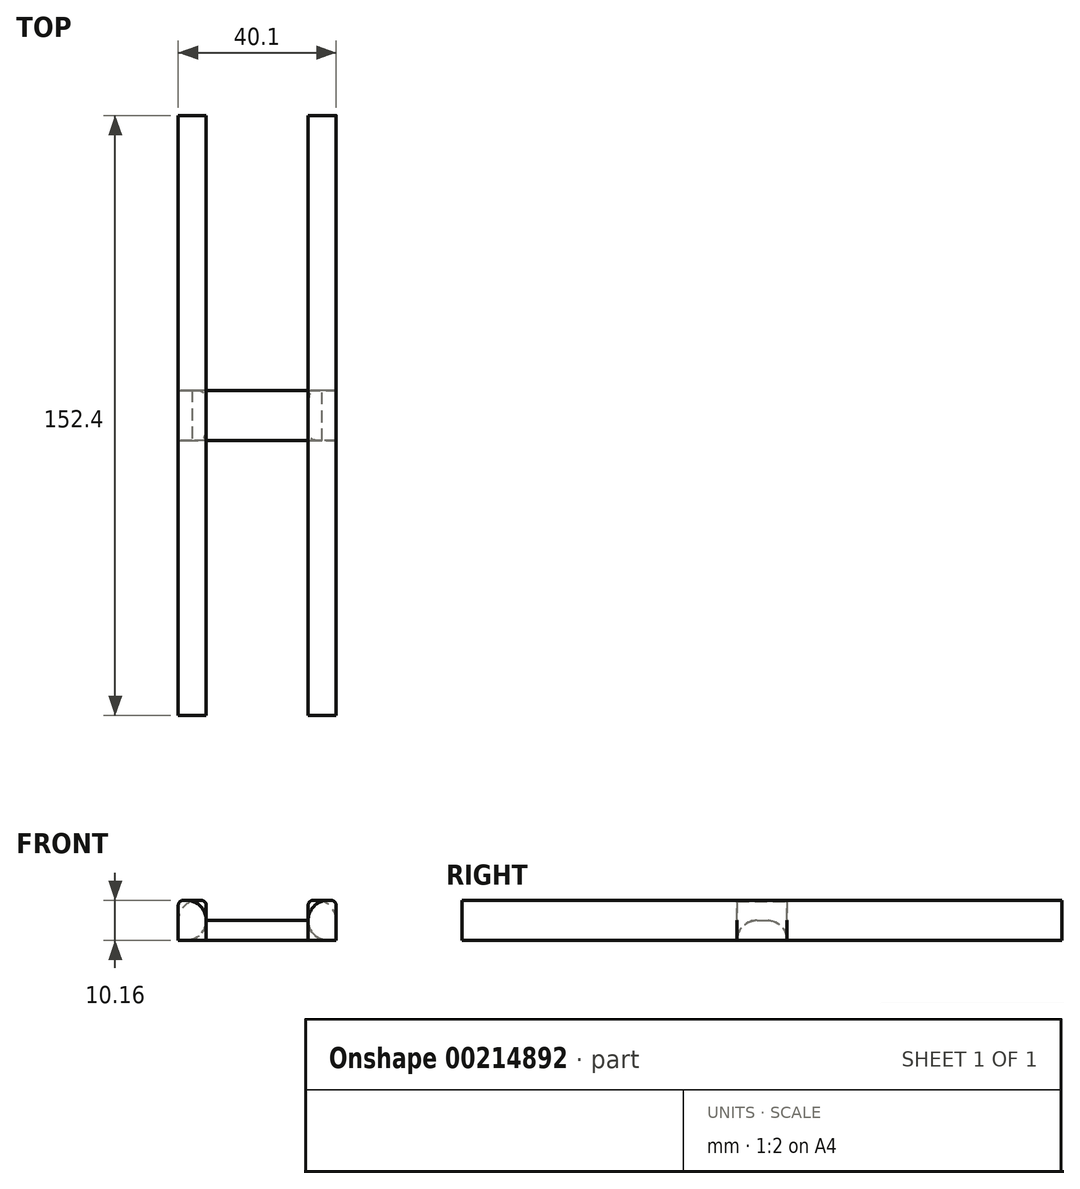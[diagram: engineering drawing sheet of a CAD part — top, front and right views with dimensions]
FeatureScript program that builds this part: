
annotation { "Feature Type Name" : "Feature", "Feature Type Description" : "" }
export const myFeature = defineFeature(function(context is Context, id is Id, definition is map)
    precondition{}
    {
        {
            var Q0;
            Q0=qCreatedBy(makeId("Front.planeOp"),FACE);
            var sketch = newSketch(context, id + "F0", { "sketchPlane" : qUnion([Q0])});
            skLineSegment(sketch, "E0.bottom", {"start": v(-45.7, 10.16) * mm, "end": v(-38.59, 10.16) * mm});
            skLineSegment(sketch, "E0.top", {"start": v(-45.7, 0) * mm, "end": v(-38.59, 0) * mm});
            skLineSegment(sketch, "E0.left", {"start": v(-45.7, 10.16) * mm, "end": v(-45.7, 0) * mm});
            skLineSegment(sketch, "E0.right", {"start": v(-38.59, 10.16) * mm, "end": v(-38.59, 0) * mm});
            skLineSegment(sketch, "E1.bottom", {"start": v(-38.59, 5.08) * mm, "end": v(-12.71, 5.08) * mm});
            skLineSegment(sketch, "E1.top", {"start": v(-38.59, 0) * mm, "end": v(-12.71, 0) * mm});
            skLineSegment(sketch, "E1.left", {"start": v(-38.59, 5.08) * mm, "end": v(-38.59, 0) * mm});
            skLineSegment(sketch, "E1.right", {"start": v(-12.71, 5.08) * mm, "end": v(-12.71, 0) * mm});
            skLineSegment(sketch, "E2.bottom", {"start": v(-12.71, 0) * mm, "end": v(-5.6, 0) * mm});
            skLineSegment(sketch, "E2.top", {"start": v(-12.71, 10.16) * mm, "end": v(-5.6, 10.16) * mm});
            skLineSegment(sketch, "E2.left", {"start": v(-12.71, 0) * mm, "end": v(-12.71, 10.16) * mm});
            skLineSegment(sketch, "E2.right", {"start": v(-5.6, 0) * mm, "end": v(-5.6, 10.16) * mm});
            skSolve(sketch);
        }
        {
            var Q0;
            Q0=makeQuery(id+"F0.imprint","IMPRINT",FACE,{"disambiguationData":[TD([[makeQuery(id+"F0.imprint","IMPRINT",EDGE,{"derivedFrom":sQuery(id+"F0.wireOp",EDGE,"E0.bottom")}),-1.0]])]});
            var Q1;
            {var subQ3=sQuery(id+"F0.wireOp",EDGE,"E2.bottom");Q1=makeQuery(id+"F0.imprint","IMPRINT",FACE,{"disambiguationData":[TD([[makeQuery(id+"F0.imprint","IMPRINT",EDGE,{"derivedFrom":subQ3}),1.0]])]});}
            extrude(context, id + "F1", {"entities" : qUnion([Q0, Q1]), "endBound" : BoundingType.SYMMETRIC, "depth" : 152.4 * mm});
        }
        {
            var Q0;
            Q0 = qSketchRegion(id + "F0", true);
            extrude(context, id + "F2", {"entities" : qUnion([Q0]), "endBound" : BoundingType.SYMMETRIC, "depth" : 12.7 * mm});
        }
        {
            var Q0;
            Q0=makeQuery(id+"F1.opExtrude","SWEPT_EDGE",EDGE,{"disambiguationData":[OSD([sQuery(id+"F0.wireOp",EDGE,"E0.bottom"),sQuery(id+"F0.wireOp",EDGE,"E0.left")])]});
            var Q1;
            Q1=makeQuery(id+"F1.opExtrude","SWEPT_EDGE",EDGE,{"disambiguationData":[OSD([sQuery(id+"F0.wireOp",EDGE,"E0.bottom"),sQuery(id+"F0.wireOp",EDGE,"E0.right")])]});
            var Q2;
            Q2=makeQuery(id+"F1.opExtrude","SWEPT_EDGE",EDGE,{"disambiguationData":[OSD([sQuery(id+"F0.wireOp",EDGE,"E2.top"),sQuery(id+"F0.wireOp",EDGE,"E2.left")])]});
            var Q3;
            Q3=makeQuery(id+"F1.opExtrude","SWEPT_EDGE",EDGE,{"disambiguationData":[OSD([sQuery(id+"F0.wireOp",EDGE,"E2.top"),sQuery(id+"F0.wireOp",EDGE,"E2.right")])]});
            fillet(context, id + "F3", {"entities" : qUnion([Q0, Q1, Q2, Q3]), "radius" : 1.27 * mm, "tangentPropagation" : true, "allowEdgeOverflow" : false});
        }
        {
            var Q0;
            Q0=makeQuery(id+"F2.opExtrude","SWEPT_EDGE",EDGE,{"disambiguationData":[OSD([sQuery(id+"F0.wireOp",EDGE,"E0.bottom"),sQuery(id+"F0.wireOp",EDGE,"E0.left")])]});
            var Q1;
            Q1=makeQuery(id+"F2.opExtrude","SWEPT_EDGE",EDGE,{"disambiguationData":[OSD([sQuery(id+"F0.wireOp",EDGE,"E0.bottom"),sQuery(id+"F0.wireOp",EDGE,"E0.right")])]});
            var Q2;
            Q2=makeQuery(id+"F2.opExtrude","SWEPT_EDGE",EDGE,{"disambiguationData":[OSD([sQuery(id+"F0.wireOp",EDGE,"E2.top"),sQuery(id+"F0.wireOp",EDGE,"E2.left")])]});
            var Q3;
            Q3=makeQuery(id+"F2.opExtrude","SWEPT_EDGE",EDGE,{"disambiguationData":[OSD([sQuery(id+"F0.wireOp",EDGE,"E2.top"),sQuery(id+"F0.wireOp",EDGE,"E2.right")])]});
            fillet(context, id + "F4", {"entities" : qUnion([Q0, Q1, Q2, Q3]), "radius" : 5.08 * mm, "tangentPropagation" : true, "allowEdgeOverflow" : false});
        }
        {
            var Q0;
            Q0=makeQuery(id+"F2.opExtrude","CAP_EDGE",EDGE,{"disambiguationData":[OSD([sQuery(id+"F0.wireOp",EDGE,"E1.bottom")])],"isStart":true});
            var Q1;
            Q1=makeQuery(id+"F2.opExtrude","CAP_EDGE",EDGE,{"disambiguationData":[OSD([sQuery(id+"F0.wireOp",EDGE,"E1.bottom")])],"isStart":false});
            fillet(context, id + "F5", {"entities" : qUnion([Q0, Q1]), "radius" : 5.08 * mm, "tangentPropagation" : true, "allowEdgeOverflow" : false});
        }
    });
